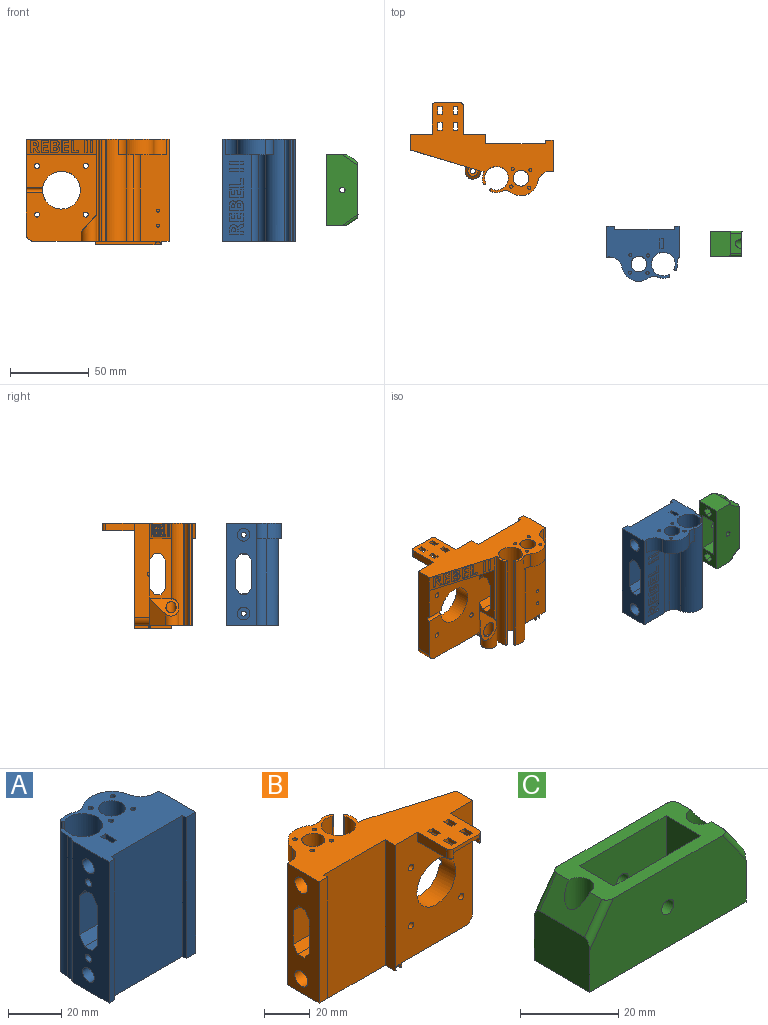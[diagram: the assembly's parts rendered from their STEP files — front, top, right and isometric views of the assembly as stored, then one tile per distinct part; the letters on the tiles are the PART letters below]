
ASSEMBLY  parts=3 mates=2
PART A: 158 faces, bbox 46x35x65 mm
  f0: plane 65x18.32mm, normal (0,1,0), area 818mm2, adj f6,f7,f8,f18,f19,f65,f66,f67
  f1: plane 65x19.5mm, normal (-1,0,0), area 955mm2, adj f8,f14,f18,f22,f39,f42,f53,f54
  f2: cylinder r=1.6mm len=3.2mm, axis (1,0,0), area 16.3mm2, adj f41,f44
  f3: cylinder r=1.6mm len=3.2mm, axis (1,0,0), area 16.3mm2, adj f40,f51
  f4: cylinder r=1.6mm len=8.88mm, axis (1,0,0), area 89.3mm2, adj f38,f43
  f5: cylinder r=1.6mm len=8.88mm, axis (1,0,0), area 89.3mm2, adj f36,f50
  f6: plane 65x19.5mm, normal (1,0,0), area 931mm2, adj f0,f8,f9,f18,f35,f37,f53,f54
  f7: cylinder r=5mm len=65mm, axis (0,0,-1), area 562.2mm2, adj f0,f8,f18,f19,f20
  f8: plane 46x33mm, normal (0,0,-1), area 837.7mm2, adj f0,f1,f6,f7,f9,f11,f12,f13
  f9: plane 65x5mm, normal (0,-1,0), area 325mm2, adj f6,f8,f17,f18
  f10: cylinder r=11mm len=17.47mm, axis (0,0,-1), area 223.9mm2, adj f18,f19,f21,f65
  f11: cylinder r=9mm len=65mm, axis (0,0,-1), area 971.4mm2, adj f8,f18,f19,f20,f21,f24
  f12: cylinder r=7.5mm len=65mm, axis (0,0,-1), area 2711.4mm2, adj f8,f18,f23,f26
  f13: cylinder r=9mm len=65mm, axis (0,0,-1), area 293.5mm2, adj f8,f18,f22,f25
  f14: plane 65x3mm, normal (0,-1,0), area 195mm2, adj f1,f8,f15,f18
  f15: plane 65x2mm, normal (1,0,0), area 130mm2, adj f8,f14,f16,f18
  f16: plane 65x38mm, normal (0,-1,0), area 2470mm2, adj f8,f15,f17,f18
  f17: plane 65x2mm, normal (-1,0,0), area 130mm2, adj f8,f9,f16,f18
  f18: plane 46x35mm, normal (0,0,1), area 1003.8mm2, adj f0,f1,f6,f7,f9,f10,f11,f12
  f19: plane 30.44x15.5mm, normal (0,0,-1), area 178.7mm2, adj f0,f7,f10,f11,f20,f21,f65
  f20: cylinder r=8mm len=55mm, axis (0,0,1), area 423.8mm2, adj f7,f8,f11,f19
  f21: cylinder r=5mm len=10mm, axis (0,0,1), area 53.9mm2, adj f10,f11,f18,f19
  f22: cylinder r=5mm len=65mm, axis (0,0,1), area 249.4mm2, adj f1,f8,f13,f18
  f23: cylinder r=1mm len=65mm, axis (0,0,-1), area 61mm2, adj f8,f12,f18,f24
  f24: cylinder r=1mm len=65mm, axis (0,0,-1), area 109.4mm2, adj f8,f11,f18,f23
  f25: cylinder r=1mm len=65mm, axis (0,0,-1), area 109.4mm2, adj f8,f13,f18,f26
  f26: cylinder r=1mm len=65mm, axis (0,0,-1), area 61mm2, adj f8,f12,f18,f25
  f27: cylinder r=1mm len=8mm, axis (0,0,1), area 50.3mm2, adj f18,f28
  f28: plane 2x2mm, normal (0,0,1), area 3.1mm2, adj f27
  f29: cylinder r=1mm len=8mm, axis (0,0,1), area 50.3mm2, adj f18,f30
  f30: plane 2x2mm, normal (0,0,1), area 3.1mm2, adj f29
  f31: cylinder r=1mm len=8mm, axis (0,0,1), area 50.3mm2, adj f18,f32
  f32: plane 2x2mm, normal (0,0,1), area 3.1mm2, adj f31
  f33: cylinder r=1mm len=8mm, axis (0,0,1), area 50.3mm2, adj f18,f34
  f34: plane 2x2mm, normal (0,0,1), area 3.1mm2, adj f33
  f35: cylinder r=4mm len=25mm, axis (1,0,0), area 628.3mm2, adj f6,f36
  f36: plane 8x8mm, normal (1,0,0), area 42.2mm2, adj f5,f35
  f37: cylinder r=4mm len=25mm, axis (1,0,0), area 628.3mm2, adj f6,f38
  f38: plane 8x8mm, normal (1,0,0), area 42.2mm2, adj f4,f37
  f39: cylinder r=3.1mm len=8mm, axis (-1,0,0), area 155.8mm2, adj f1,f40
  f40: plane 6.2x6.2mm, normal (-1,0,0), area 22.1mm2, adj f3,f39
  f41: plane 6.2x6.2mm, normal (-1,0,0), area 22.1mm2, adj f2,f42
  f42: cylinder r=3.1mm len=8mm, axis (-1,0,0), area 155.8mm2, adj f1,f41
  f43: plane 10.5x6mm, normal (-1,0,0), area 55mm2, adj f4,f18,f45,f46,f47
  f44: plane 10.5x6mm, normal (1,0,0), area 55mm2, adj f2,f18,f45,f46,f47
  f45: plane 10.5x2.5mm, normal (0,-1,0), area 26.3mm2, adj f18,f43,f44,f47
  f46: plane 10.5x2.5mm, normal (0,1,0), area 26.3mm2, adj f18,f43,f44,f47
  f47: plane 6x2.5mm, normal (0,0,1), area 15mm2, adj f43,f44,f45,f46
  f48: plane 10.5x2.5mm, normal (0,-1,0), area 26.3mm2, adj f8,f50,f51,f52
  f49: plane 10.5x2.5mm, normal (0,1,0), area 26.3mm2, adj f8,f50,f51,f52
  f50: plane 10.5x6mm, normal (-1,0,0), area 55mm2, adj f5,f8,f48,f49,f52
  f51: plane 10.5x6mm, normal (1,0,0), area 55mm2, adj f3,f8,f48,f49,f52
  f52: plane 6x2.5mm, normal (0,0,-1), area 15mm2, adj f48,f49,f50,f51
  f53: plane 46x17.98mm, normal (0,1,0), area 827.1mm2, adj f1,f6,f54,f58
  f54: plane 46x4.01mm, normal (0,0.8,0.6), area 230.4mm2, adj f1,f6,f53,f55
  f55: plane 46x4mm, normal (0,0,1), area 184mm2, adj f1,f6,f54,f56
  f56: plane 46x3.99mm, normal (0,-0.8,0.6), area 229.5mm2, adj f1,f6,f55,f57
  f57: plane 46x18.03mm, normal (0,-1,0), area 829.3mm2, adj f1,f6,f56,f59
  f58: plane 46x4.01mm, normal (0,0.8,-0.6), area 230.4mm2, adj f1,f6,f53,f60
  f59: plane 46x3.99mm, normal (0,-0.8,-0.6), area 229.5mm2, adj f1,f6,f57,f60
  f60: plane 46x4mm, normal (0,0,-1), area 184mm2, adj f1,f6,f58,f59
  f61: cylinder r=1.6mm len=10mm, axis (-1,0,0), area 100.5mm2, adj f1,f62
  f62: plane 3.2x3.2mm, normal (-1,0,0), area 8mm2, adj f61
  f63: cylinder r=1.6mm len=10mm, axis (-1,0,0), area 100.5mm2, adj f1,f64
  f64: plane 3.2x3.2mm, normal (-1,0,0), area 8mm2, adj f63
  f65: cylinder r=8mm len=10mm, axis (0,0,-1), area 110.8mm2, adj f0,f10,f18,f19
  f66: plane 5.02x0.5mm, normal (1,0,0), area 2.5mm2, adj f0,f67,f77,f78
  f67: plane 1.53x0.5mm, normal (0,0,-1), area 0.8mm2, adj f0,f66,f68,f78
  f68: plane 3.17x0.5mm, normal (-1,0,0), area 1.6mm2, adj f0,f67,f69,f78
  f69: plane 2.25x0.5mm, normal (0,0,-1), area 1.1mm2, adj f0,f68,f70,f78
  f70: plane 2.95x0.5mm, normal (1,0,0), area 1.5mm2, adj f0,f69,f71,f78
  f71: plane 1.52x0.5mm, normal (0,0,-1), area 0.8mm2, adj f0,f70,f72,f78
  f72: plane 2.95x0.5mm, normal (-1,0,0), area 1.5mm2, adj f0,f71,f73,f78
  f73: plane 1.92x0.5mm, normal (0,0,-1), area 1mm2, adj f0,f72,f74,f78
  f74: plane 3.17x0.5mm, normal (1,0,0), area 1.6mm2, adj f0,f73,f75,f78
  f75: plane 1.52x0.5mm, normal (0,0,-1), area 0.8mm2, adj f0,f74,f76,f78
  f76: plane 5.02x0.5mm, normal (-1,0,0), area 2.5mm2, adj f0,f75,f77,f78
  f77: plane 8.73x0.5mm, normal (0,0,1), area 4.4mm2, adj f0,f66,f76,f78
  f78: plane 8.73x5.02mm, normal (0,1,0), area 30.3mm2, adj f66,f67,f68,f69,f70,f71,f72,f73
  f79: plane 5.02x0.5mm, normal (1,0,0), area 2.5mm2, adj f0,f80,f90,f91
  f80: plane 1.53x0.5mm, normal (0,0,-1), area 0.8mm2, adj f0,f79,f81,f91
  f81: plane 3.17x0.5mm, normal (-1,0,0), area 1.6mm2, adj f0,f80,f82,f91
  f82: plane 2.25x0.5mm, normal (0,0,-1), area 1.1mm2, adj f0,f81,f83,f91
  f83: plane 2.95x0.5mm, normal (1,0,0), area 1.5mm2, adj f0,f82,f84,f91
  f84: plane 1.52x0.5mm, normal (0,0,-1), area 0.8mm2, adj f0,f83,f85,f91
  f85: plane 2.95x0.5mm, normal (-1,0,0), area 1.5mm2, adj f0,f84,f86,f91
  f86: plane 1.92x0.5mm, normal (0,0,-1), area 1mm2, adj f0,f85,f87,f91
  f87: plane 3.17x0.5mm, normal (1,0,0), area 1.6mm2, adj f0,f86,f88,f91
  f88: plane 1.52x0.5mm, normal (0,0,-1), area 0.8mm2, adj f0,f87,f89,f91
  f89: plane 5.02x0.5mm, normal (-1,0,0), area 2.5mm2, adj f0,f88,f90,f91
  f90: plane 8.73x0.5mm, normal (0,0,1), area 4.4mm2, adj f0,f79,f89,f91
  f91: plane 8.73x5.02mm, normal (0,1,0), area 30.3mm2, adj f79,f80,f81,f82,f83,f84,f85,f86
  f92: plane 8.73x0.5mm, normal (0,0,1), area 4.4mm2, adj f0,f93,f97,f98
  f93: plane 5.39x0.5mm, normal (1,0,0), area 2.7mm2, adj f0,f92,f94,f98
  f94: plane 1.53x0.5mm, normal (0,0,-1), area 0.8mm2, adj f0,f93,f95,f98
  f95: plane 3.54x0.5mm, normal (-1,0,0), area 1.8mm2, adj f0,f94,f96,f98
  f96: plane 7.2x0.5mm, normal (0,0,-1), area 3.6mm2, adj f0,f95,f97,f98
  f97: plane 1.85x0.5mm, normal (-1,0,0), area 0.9mm2, adj f0,f92,f96,f98
  f98: plane 8.73x5.39mm, normal (0,1,0), area 21.6mm2, adj f92,f93,f94,f95,f96,f97
  f99: plane 8.73x0.5mm, normal (0,0,1), area 4.4mm2, adj f0,f100,f102,f103
  f100: plane 1.85x0.5mm, normal (1,0,0), area 0.9mm2, adj f0,f99,f101,f103
  f101: plane 8.73x0.5mm, normal (0,0,-1), area 4.4mm2, adj f0,f100,f102,f103
  f102: plane 1.85x0.5mm, normal (-1,0,0), area 0.9mm2, adj f0,f99,f101,f103
  f103: plane 8.73x1.85mm, normal (0,1,0), area 16.1mm2, adj f99,f100,f101,f102
  f104: plane 8.73x0.5mm, normal (0,0,1), area 4.4mm2, adj f0,f105,f107,f108
  f105: plane 1.85x0.5mm, normal (1,0,0), area 0.9mm2, adj f0,f104,f106,f108
  f106: plane 8.73x0.5mm, normal (0,0,-1), area 4.4mm2, adj f0,f105,f107,f108
  f107: plane 1.85x0.5mm, normal (-1,0,0), area 0.9mm2, adj f0,f104,f106,f108
  f108: plane 8.73x1.85mm, normal (0,1,0), area 16.1mm2, adj f104,f105,f106,f107
  f109: plane 3.35x0.5mm, normal (0,0,-1), area 1.7mm2, adj f0,f110,f127,f128
  f110: plane 0.98x0.5mm, normal (1,0,0), area 0.5mm2, adj f0,f109,f111,f128
  f111: plane 3.35x2.08mm, normal (0.53,0,0.85), area 2mm2, adj f0,f110,f112,f128
  f112: plane 2.05x0.5mm, normal (1,0,0), area 1mm2, adj f0,f111,f113,f128
  f113: extruded ~3.8x2.57mm, area 2.3mm2, adj f0,f112,f114,f128
  f114: extruded ~1.2x0.94mm, area 0.8mm2, adj f0,f113,f115,f128
  f115: extruded ~1.37x0.5mm, area 0.7mm2, adj f0,f114,f116,f128
  f116: extruded ~1.97x0.85mm, area 1.1mm2, adj f0,f115,f117,f128
  f117: extruded ~2.63x0.65mm, area 1.4mm2, adj f0,f116,f118,f128
  f118: plane 2.54x0.5mm, normal (-1,0,0), area 1.3mm2, adj f0,f117,f119,f128
  f119: plane 8.73x0.5mm, normal (0,0,1), area 4.4mm2, adj f0,f118,f127,f128
  f120: plane 0.6x0.5mm, normal (-1,0,0), area 0.3mm2, adj f121,f126,f128,f129
  f121: plane 2.36x0.5mm, normal (0,0,-1), area 1.2mm2, adj f120,f122,f128,f129
  f122: plane 0.56x0.5mm, normal (1,0,0), area 0.3mm2, adj f121,f123,f128,f129
  f123: extruded ~1.32x0.5mm, area 0.7mm2, adj f122,f124,f128,f129
  f124: extruded ~0.88x0.5mm, area 0.5mm2, adj f123,f125,f128,f129
  f125: extruded ~0.92x0.5mm, area 0.5mm2, adj f124,f126,f128,f129
  f126: extruded ~1.3x0.5mm, area 0.7mm2, adj f120,f125,f128,f129
  f127: plane 1.85x0.5mm, normal (1,0,0), area 0.9mm2, adj f0,f109,f119,f128
  f128: plane 8.73x6.97mm, normal (0,1,0), area 37.2mm2, adj f109,f110,f111,f112,f113,f114,f115,f116
  f129: plane 2.36x2.31mm, normal (0,1,0), area 4.8mm2, adj f120,f121,f122,f123,f124,f125,f126
  f130: plane 2.27x0.5mm, normal (0,0,-1), area 1.1mm2, adj f131,f154,f155,f157
  f131: plane 1.15x0.5mm, normal (1,0,0), area 0.6mm2, adj f130,f132,f155,f157
  f132: extruded ~1.55x1.09mm, area 1.1mm2, adj f131,f133,f155,f157
  f133: extruded ~0.9x0.5mm, area 0.5mm2, adj f132,f134,f155,f157
  f134: extruded ~1.13x0.5mm, area 0.6mm2, adj f133,f154,f155,f157
  f135: plane 1.07x0.5mm, normal (-1,0,0), area 0.5mm2, adj f136,f152,f155,f156
  f136: plane 1.94x0.5mm, normal (0,0,-1), area 1mm2, adj f135,f137,f155,f156
  f137: plane 0.97x0.5mm, normal (1,0,0), area 0.5mm2, adj f136,f138,f155,f156
  f138: extruded ~1.16x0.5mm, area 0.6mm2, adj f137,f139,f155,f156
  f139: extruded ~0.72x0.5mm, area 0.4mm2, adj f138,f140,f155,f156
  f140: extruded ~0.77x0.5mm, area 0.4mm2, adj f139,f152,f155,f156
  f141: plane 2.72x0.5mm, normal (-1,0,0), area 1.4mm2, adj f0,f142,f153,f155
  f142: plane 8.73x0.5mm, normal (0,0,1), area 4.4mm2, adj f0,f141,f143,f155
  f143: plane 3.26x0.5mm, normal (1,0,0), area 1.6mm2, adj f0,f142,f144,f155
  f144: extruded ~2.34x0.67mm, area 1.2mm2, adj f0,f143,f145,f155
  f145: extruded ~1.86x0.86mm, area 1.1mm2, adj f0,f144,f146,f155
  f146: extruded ~1.35x0.5mm, area 0.7mm2, adj f0,f145,f147,f155
  f147: extruded ~1.2x0.69mm, area 0.7mm2, adj f0,f146,f148,f155
  f148: plane 0.5x0.06mm, normal (0,0,-1), area 0mm2, adj f0,f147,f149,f155
  f149: extruded ~0.98x0.6mm, area 0.6mm2, adj f0,f148,f150,f155
  f150: extruded ~1.28x0.5mm, area 0.7mm2, adj f0,f149,f151,f155
  f151: extruded ~1.68x0.84mm, area 1mm2, adj f0,f150,f153,f155
  f152: extruded ~1.09x0.5mm, area 0.6mm2, adj f135,f140,f155,f156
  f153: extruded ~2.69x0.53mm, area 1.4mm2, adj f0,f141,f151,f155
  f154: plane 1.21x0.5mm, normal (-1,0,0), area 0.6mm2, adj f130,f134,f155,f157
  f155: plane 8.73x6.47mm, normal (0,1,0), area 41.5mm2, adj f130,f131,f132,f133,f134,f135,f136,f137
  f156: plane 2.5x1.94mm, normal (0,1,0), area 4.4mm2, adj f135,f136,f137,f138,f139,f140,f152
  f157: plane 2.7x2.27mm, normal (0,1,0), area 5.6mm2, adj f130,f131,f132,f133,f134,f154
PART B: 213 faces, bbox 92.5x60.6x69.2 mm
  f0: plane 39x23.85mm, normal (0,0,-1), area 44.3mm2, adj f1,f20,f23,f24,f194,f197,f198,f202
  f1: plane 67.3x48mm, normal (0,-1,0), area 2581.9mm2, adj f0,f3,f4,f7,f8,f15,f24,f25
  f2: plane 1.73x0.24mm, normal (-1,0,0), area 0.3mm2, adj f3,f197,f203,f204,f205
  f3: plane 39.1x23.87mm, normal (0,0,-1), area 44.1mm2, adj f1,f2,f20,f195,f196,f197,f199,f202
  f4: plane 39x10mm, normal (0,0,-1), area 390mm2, adj f1,f17,f76,f199
  f5: plane 47x27mm, normal (0,0,-1), area 619.3mm2, adj f10,f11,f19,f20,f26,f27,f28,f29
  f6: plane 19.5x5mm, normal (0,0,-1), area 97.5mm2, adj f18,f20,f21,f22,f194
  f7: plane 91x59.06mm, normal (0,0,1), area 2120.1mm2, adj f1,f9,f14,f18,f19,f20,f21,f22
  f8: plane 20x16mm, normal (0,0,-1), area 260mm2, adj f1,f14,f69,f70,f178,f179,f180,f181
  f9: plane 45x13.5mm, normal (0.29,0.96,0), area 301.8mm2, adj f7,f25,f26,f63,f86,f87,f88,f89
  f10: plane 17x10.24mm, normal (0.76,-0.65,0), area 163.6mm2, adj f5,f11,f17,f85,f200
  f11: cylinder r=5mm len=17mm, axis (0,0,-1), area 202.3mm2, adj f5,f10,f26,f85
  f12: cylinder r=3.25mm len=10.06mm, axis (0,0,1), area 131.6mm2, adj f84,f85
  f13: cylinder r=1.6mm len=3.2mm, axis (0,0,-1), area 20.1mm2, adj f77,f84
  f14: plane 16x2mm, normal (0,-1,0), area 32mm2, adj f7,f8,f67,f68
  f15: plane 20x2mm, normal (0,0,-1), area 39.1mm2, adj f1,f65,f68,f70
  f16: plane 38x13.5mm, normal (1,0,0), area 277mm2, adj f17,f26,f51,f52,f53,f54,f55,f56
  f17: plane 91x55mm, normal (0,1,0), area 2781.5mm2, adj f4,f10,f16,f18,f25,f51,f57,f58
  f18: plane 65x19.5mm, normal (-1,0,0), area 931mm2, adj f6,f7,f17,f20,f21,f47,f49,f51
  f19: cylinder r=5mm len=65mm, axis (0,0,-1), area 548mm2, adj f5,f7,f20,f31,f32
  f20: plane 67.3x18.44mm, normal (0,1,0), area 1029.3mm2, adj f0,f3,f5,f6,f7,f18,f19,f31
  f21: plane 65x5mm, normal (0,-1,0), area 325mm2, adj f6,f7,f18,f22
  f22: plane 65x2.06mm, normal (1,0,0), area 133.6mm2, adj f6,f7,f21,f23
  f23: plane 67.3x38mm, normal (0,-1,0), area 2557.4mm2, adj f0,f7,f22,f24,f194
  f24: plane 67.3x6.06mm, normal (-1,0,0), area 407.5mm2, adj f0,f1,f7,f23
  f25: plane 60x10mm, normal (1,0,0), area 596.5mm2, adj f1,f7,f9,f17,f75,f76
  f26: plane 65x2.24mm, normal (0,1,0), area 145.5mm2, adj f5,f7,f9,f11,f16,f27
  f27: cylinder r=9mm len=65mm, axis (0,0,-1), area 538.6mm2, adj f5,f7,f26,f44
  f28: cylinder r=7.5mm len=65mm, axis (0,0,-1), area 2711.3mm2, adj f5,f7,f43,f46
  f29: cylinder r=9mm len=65mm, axis (0,0,-1), area 977.8mm2, adj f5,f7,f31,f32,f33,f45
  f30: cylinder r=11mm len=17.48mm, axis (0,0,-1), area 224.3mm2, adj f7,f31,f33,f34
  f31: plane 30.45x15.56mm, normal (0,0,-1), area 179.2mm2, adj f19,f20,f29,f30,f32,f33,f34
  f32: cylinder r=8mm len=55mm, axis (0,0,1), area 430.9mm2, adj f5,f19,f29,f31
  f33: cylinder r=5mm len=10mm, axis (0,0,1), area 53.9mm2, adj f7,f29,f30,f31
  f34: cylinder r=8mm len=10mm, axis (0,0,-1), area 111.1mm2, adj f7,f20,f30,f31
  f35: cylinder r=1mm len=8mm, axis (0,0,1), area 50.3mm2, adj f7,f36
  f36: plane 2x2mm, normal (0,0,1), area 3.1mm2, adj f35
  f37: cylinder r=1mm len=8mm, axis (0,0,1), area 50.3mm2, adj f7,f38
  f38: plane 2x2mm, normal (0,0,1), area 3.1mm2, adj f37
  f39: cylinder r=1mm len=8mm, axis (0,0,1), area 50.3mm2, adj f7,f40
  f40: plane 2x2mm, normal (0,0,1), area 3.1mm2, adj f39
  f41: cylinder r=1mm len=8mm, axis (0,0,1), area 50.3mm2, adj f7,f42
  f42: plane 2x2mm, normal (0,0,1), area 3.1mm2, adj f41
  f43: cylinder r=1mm len=65mm, axis (0,0,-1), area 60.2mm2, adj f5,f7,f28,f44
  f44: cylinder r=1mm len=65mm, axis (0,0,-1), area 110.1mm2, adj f5,f7,f27,f43
  f45: cylinder r=1mm len=65mm, axis (0,0,-1), area 108.8mm2, adj f5,f7,f29,f46
  f46: cylinder r=1mm len=65mm, axis (0,0,-1), area 61.7mm2, adj f5,f7,f28,f45
  f47: cylinder r=4mm len=25mm, axis (-1,0,0), area 628.3mm2, adj f18,f48
  f48: plane 8x8mm, normal (-1,0,0), area 50.3mm2, adj f47
  f49: cylinder r=4mm len=25mm, axis (-1,0,0), area 628.3mm2, adj f18,f50
  f50: plane 8x8mm, normal (-1,0,0), area 50.3mm2, adj f49
  f51: plane 46x4mm, normal (0,0.81,-0.59), area 227.8mm2, adj f16,f17,f18,f52
  f52: plane 46x4mm, normal (0,0,-1), area 184mm2, adj f16,f18,f51,f53
  f53: plane 46x4mm, normal (0,-0.79,-0.61), area 232.2mm2, adj f16,f18,f52,f54
  f54: plane 46x18mm, normal (0,-1,0), area 828mm2, adj f16,f18,f53,f55
  f55: plane 46x4mm, normal (0,-0.81,0.59), area 227.8mm2, adj f16,f18,f54,f56
  f56: plane 46x4mm, normal (0,0,1), area 184mm2, adj f16,f18,f55,f57
  f57: plane 46x4mm, normal (0,0.79,0.61), area 232.2mm2, adj f16,f17,f18,f56
  f58: cylinder r=1.6mm len=10mm, axis (0,-1,0), area 100.5mm2, adj f1,f17
  f59: cylinder r=1.6mm len=10mm, axis (0,-1,0), area 100.5mm2, adj f1,f17
  f60: cylinder r=12mm len=24mm, axis (0,-1,0), area 754mm2, adj f1,f17,f75
  f61: cylinder r=1.6mm len=10mm, axis (0,-1,0), area 100.5mm2, adj f1,f17
  f62: cylinder r=1.6mm len=10mm, axis (0,-1,0), area 100.5mm2, adj f1,f17
  f63: plane 45x13.5mm, normal (0,0,-1), area 303.8mm2, adj f9,f16,f17
  f64: plane 18x5mm, normal (-1,0,0), area 90mm2, adj f1,f7,f66,f67
  f65: plane 18x5mm, normal (1,0,0), area 90mm2, adj f1,f7,f15,f68
  f66: plane 20x2mm, normal (0,0,-1), area 39.1mm2, adj f1,f64,f67,f69
  f67: cylinder r=2mm len=5mm, axis (0,0,1), area 15.7mm2, adj f7,f14,f64,f66,f69
  f68: cylinder r=2mm len=5mm, axis (0,0,1), area 15.7mm2, adj f7,f14,f15,f65,f70
  f69: plane 20x3mm, normal (1,0,0), area 60mm2, adj f1,f8,f66,f67
  f70: plane 20x3mm, normal (-1,0,0), area 60mm2, adj f1,f8,f15,f68
  f71: cylinder r=1mm len=4mm, axis (0,1,0), area 25.1mm2, adj f20,f72
  f72: plane 2x2mm, normal (0,1,0), area 3.1mm2, adj f71
  f73: cylinder r=1mm len=4mm, axis (0,1,0), area 25.1mm2, adj f20,f74
  f74: plane 2x2mm, normal (0,1,0), area 3.1mm2, adj f73
  f75: cylinder r=1.5mm len=10.59mm, axis (1,0,0), area 49.9mm2, adj f17,f25,f60
  f76: cylinder r=5mm len=10mm, axis (0,1,0), area 78.5mm2, adj f1,f4,f17,f25
  f77: plane 5.98x5.83mm, normal (0,0,-1), area 16.3mm2, adj f13,f78,f79,f80,f81,f82,f83
  f78: plane 3x2.99mm, normal (-0.21,-0.98,0), area 9.2mm2, adj f5,f77,f79,f83
  f79: plane 3x2.92mm, normal (-0.95,-0.3,0), area 9.2mm2, adj f5,f77,f78,f80
  f80: plane 3x2.26mm, normal (-0.74,0.67,0), area 9.2mm2, adj f5,f77,f79,f81
  f81: plane 3x2.99mm, normal (0.21,0.98,0), area 9.2mm2, adj f5,f77,f80,f82
  f82: plane 3x2.92mm, normal (0.95,0.3,0), area 9.2mm2, adj f5,f77,f81,f83
  f83: plane 3x2.26mm, normal (0.74,-0.67,0), area 9.2mm2, adj f5,f77,f78,f82
  f84: plane 6.5x6.5mm, normal (0,0,1), area 25.1mm2, adj f12,f13
  f85: plane 20.02x12.62mm, normal (0.74,0,0.67), area 123.2mm2, adj f10,f11,f12,f16
  f86: plane 4.47x1.78mm, normal (0,0,1), area 2.3mm2, adj f9,f87,f97,f98
  f87: plane 1.37x0.48mm, normal (0.96,-0.29,0), area 0.7mm2, adj f9,f86,f88,f98
  f88: plane 2.88x1.3mm, normal (0,0,-1), area 1.4mm2, adj f9,f87,f89,f98
  f89: plane 2.02x0.48mm, normal (0.96,-0.29,0), area 1mm2, adj f9,f88,f90,f98
  f90: plane 2.69x1.24mm, normal (0,0,1), area 1.3mm2, adj f9,f89,f91,f98
  f91: plane 1.36x0.48mm, normal (0.96,-0.29,0), area 0.7mm2, adj f9,f90,f92,f98
  f92: plane 2.69x1.24mm, normal (0,0,-1), area 1.3mm2, adj f9,f91,f93,f98
  f93: plane 1.72x0.48mm, normal (0.96,-0.29,0), area 0.9mm2, adj f9,f92,f94,f98
  f94: plane 2.88x1.3mm, normal (0,0,1), area 1.4mm2, adj f9,f93,f95,f98
  f95: plane 1.36x0.48mm, normal (0.96,-0.29,0), area 0.7mm2, adj f9,f94,f96,f98
  f96: plane 4.47x1.78mm, normal (0,0,-1), area 2.3mm2, adj f9,f95,f97,f98
  f97: plane 7.84x0.48mm, normal (-0.96,0.29,0), area 3.9mm2, adj f9,f86,f96,f98
  f98: plane 7.84x4.33mm, normal (0.29,0.96,0), area 24.5mm2, adj f86,f87,f88,f89,f90,f91,f92,f93
  f99: plane 4.47x1.78mm, normal (0,0,1), area 2.3mm2, adj f9,f100,f110,f111
  f100: plane 1.37x0.48mm, normal (0.96,-0.29,0), area 0.7mm2, adj f9,f99,f101,f111
  f101: plane 2.88x1.3mm, normal (0,0,-1), area 1.4mm2, adj f9,f100,f102,f111
  f102: plane 2.02x0.48mm, normal (0.96,-0.29,0), area 1mm2, adj f9,f101,f103,f111
  f103: plane 2.69x1.24mm, normal (0,0,1), area 1.3mm2, adj f9,f102,f104,f111
  f104: plane 1.36x0.48mm, normal (0.96,-0.29,0), area 0.7mm2, adj f9,f103,f105,f111
  f105: plane 2.69x1.24mm, normal (0,0,-1), area 1.3mm2, adj f9,f104,f106,f111
  f106: plane 1.72x0.48mm, normal (0.96,-0.29,0), area 0.9mm2, adj f9,f105,f107,f111
  f107: plane 2.88x1.3mm, normal (0,0,1), area 1.4mm2, adj f9,f106,f108,f111
  f108: plane 1.36x0.48mm, normal (0.96,-0.29,0), area 0.7mm2, adj f9,f107,f109,f111
  f109: plane 4.47x1.78mm, normal (0,0,-1), area 2.3mm2, adj f9,f108,f110,f111
  f110: plane 7.84x0.48mm, normal (-0.96,0.29,0), area 3.9mm2, adj f9,f99,f109,f111
  f111: plane 7.84x4.33mm, normal (0.29,0.96,0), area 24.5mm2, adj f99,f100,f101,f102,f103,f104,f105,f106
  f112: plane 7.84x0.48mm, normal (-0.96,0.29,0), area 3.9mm2, adj f9,f113,f117,f118
  f113: plane 4.78x1.87mm, normal (0,0,1), area 2.4mm2, adj f9,f112,f114,f118
  f114: plane 1.37x0.48mm, normal (0.96,-0.29,0), area 0.7mm2, adj f9,f113,f115,f118
  f115: plane 3.19x1.39mm, normal (0,0,-1), area 1.6mm2, adj f9,f114,f116,f118
  f116: plane 6.47x0.48mm, normal (0.96,-0.29,0), area 3.2mm2, adj f9,f115,f117,f118
  f117: plane 1.74x0.96mm, normal (0,0,-1), area 0.8mm2, adj f9,f112,f116,f118
  f118: plane 7.84x4.64mm, normal (0.29,0.96,0), area 17.4mm2, adj f112,f113,f114,f115,f116,f117
  f119: plane 7.84x0.48mm, normal (-0.96,0.29,0), area 3.9mm2, adj f9,f120,f122,f123
  f120: plane 1.74x0.96mm, normal (0,0,1), area 0.8mm2, adj f9,f119,f121,f123
  f121: plane 7.84x0.48mm, normal (0.96,-0.29,0), area 3.9mm2, adj f9,f120,f122,f123
  f122: plane 1.74x0.96mm, normal (0,0,-1), area 0.8mm2, adj f9,f119,f121,f123
  f123: plane 7.84x1.59mm, normal (0.29,0.96,0), area 13mm2, adj f119,f120,f121,f122
  f124: plane 7.84x0.48mm, normal (-0.96,0.29,0), area 3.9mm2, adj f9,f125,f127,f128
  f125: plane 1.74x0.96mm, normal (0,0,1), area 0.8mm2, adj f9,f124,f126,f128
  f126: plane 7.84x0.48mm, normal (0.96,-0.29,0), area 3.9mm2, adj f9,f125,f127,f128
  f127: plane 1.74x0.96mm, normal (0,0,-1), area 0.8mm2, adj f9,f124,f126,f128
  f128: plane 7.84x1.59mm, normal (0.29,0.96,0), area 13mm2, adj f124,f125,f126,f127
  f129: plane 3.01x0.48mm, normal (0.96,-0.29,0), area 1.5mm2, adj f9,f130,f147,f148
  f130: plane 0.99x0.73mm, normal (0,0,1), area 0.4mm2, adj f9,f129,f131,f148
  f131: plane 3.01x1.94mm, normal (-0.81,0.24,0.53), area 1.8mm2, adj f9,f130,f132,f148
  f132: plane 1.91x1.01mm, normal (0,0,1), area 0.9mm2, adj f9,f131,f133,f148
  f133: extruded ~3.42x2.35mm, area 2.1mm2, adj f9,f132,f134,f148
  f134: extruded ~1.18x0.84mm, area 0.7mm2, adj f9,f133,f135,f148
  f135: extruded ~1.23x0.59mm, area 0.7mm2, adj f9,f134,f136,f148
  f136: extruded ~1.77x0.88mm, area 1mm2, adj f9,f135,f137,f148
  f137: extruded ~2.41x1.16mm, area 1.2mm2, adj f9,f136,f138,f148
  f138: plane 2.33x1.14mm, normal (0,0,-1), area 1.1mm2, adj f9,f137,f139,f148
  f139: plane 7.84x0.48mm, normal (-0.96,0.29,0), area 3.9mm2, adj f9,f138,f147,f148
  f140: plane 0.66x0.63mm, normal (0,0,-1), area 0.3mm2, adj f141,f146,f148,f149
  f141: plane 2.12x0.48mm, normal (0.96,-0.29,0), area 1.1mm2, adj f140,f142,f148,f149
  f142: plane 0.63x0.62mm, normal (0,0,1), area 0.3mm2, adj f141,f143,f148,f149
  f143: extruded ~1.28x0.82mm, area 0.6mm2, adj f142,f144,f148,f149
  f144: extruded ~0.79x0.59mm, area 0.5mm2, adj f143,f145,f148,f149
  f145: extruded ~0.83x0.59mm, area 0.5mm2, adj f144,f146,f148,f149
  f146: extruded ~1.26x0.81mm, area 0.6mm2, adj f140,f145,f148,f149
  f147: plane 1.74x0.96mm, normal (0,0,1), area 0.8mm2, adj f9,f129,f139,f148
  f148: plane 7.84x6mm, normal (0.29,0.96,0), area 30mm2, adj f129,f130,f131,f132,f133,f134,f135,f136
  f149: plane 2.12x1.99mm, normal (0.29,0.96,0), area 3.9mm2, adj f140,f141,f142,f143,f144,f145,f146
  f150: plane 2.04x0.48mm, normal (0.96,-0.29,0), area 1mm2, adj f151,f174,f175,f177
  f151: plane 1.13x0.78mm, normal (0,0,1), area 0.5mm2, adj f150,f152,f175,f177
  f152: extruded ~1.48x0.98mm, area 1mm2, adj f151,f153,f175,f177
  f153: extruded ~0.81x0.57mm, area 0.5mm2, adj f152,f154,f175,f177
  f154: extruded ~1.11x0.77mm, area 0.5mm2, adj f153,f174,f175,f177
  f155: plane 1.07x0.76mm, normal (0,0,-1), area 0.5mm2, adj f156,f172,f175,f176
  f156: plane 1.74x0.48mm, normal (0.96,-0.29,0), area 0.9mm2, adj f155,f157,f175,f176
  f157: plane 0.98x0.73mm, normal (0,0,1), area 0.4mm2, adj f156,f158,f175,f176
  f158: extruded ~1.14x0.78mm, area 0.5mm2, adj f157,f159,f175,f176
  f159: extruded ~0.65x0.57mm, area 0.4mm2, adj f158,f160,f175,f176
  f160: extruded ~0.69x0.57mm, area 0.4mm2, adj f159,f172,f175,f176
  f161: plane 2.48x1.18mm, normal (0,0,-1), area 1.2mm2, adj f9,f162,f173,f175
  f162: plane 7.84x0.48mm, normal (-0.96,0.29,0), area 3.9mm2, adj f9,f161,f163,f175
  f163: plane 2.95x1.32mm, normal (0,0,1), area 1.5mm2, adj f9,f162,f164,f175
  f164: extruded ~2.16x1.08mm, area 1.1mm2, adj f9,f163,f165,f175
  f165: extruded ~1.67x0.89mm, area 1mm2, adj f9,f164,f166,f175
  f166: extruded ~1.21x0.57mm, area 0.6mm2, adj f9,f165,f167,f175
  f167: extruded ~1.17x0.79mm, area 0.6mm2, adj f9,f166,f168,f175
  f168: plane 0.48x0.14mm, normal (0.96,-0.29,0), area 0mm2, adj f9,f167,f169,f175
  f169: extruded ~0.98x0.73mm, area 0.5mm2, adj f9,f168,f170,f175
  f170: extruded ~1.15x0.57mm, area 0.6mm2, adj f9,f169,f171,f175
  f171: extruded ~1.51x0.87mm, area 0.9mm2, adj f9,f170,f173,f175
  f172: extruded ~1.08x0.76mm, area 0.5mm2, adj f155,f160,f175,f176
  f173: extruded ~2.46x1.18mm, area 1.2mm2, adj f9,f161,f171,f175
  f174: plane 1.18x0.79mm, normal (0,0,-1), area 0.5mm2, adj f150,f154,f175,f177
  f175: plane 7.84x5.57mm, normal (0.29,0.96,0), area 33.5mm2, adj f150,f151,f152,f153,f154,f155,f156,f157
  f176: plane 2.15x1.74mm, normal (0.29,0.96,0), area 3.6mm2, adj f155,f156,f157,f158,f159,f160,f172
  f177: plane 2.32x2.04mm, normal (0.29,0.96,0), area 4.5mm2, adj f150,f151,f152,f153,f154,f174
  f178: plane 3x2mm, normal (0,1,0), area 6mm2, adj f7,f8,f179,f181
  f179: plane 5x2mm, normal (-1,0,0), area 10mm2, adj f7,f8,f178,f180
  f180: plane 3x2mm, normal (0,-1,0), area 6mm2, adj f7,f8,f179,f181
  f181: plane 5x2mm, normal (1,0,0), area 10mm2, adj f7,f8,f178,f180
  f182: plane 5x2mm, normal (1,0,0), area 10mm2, adj f7,f8,f183,f184
  f183: plane 3x2mm, normal (0,-1,0), area 6mm2, adj f7,f8,f182,f185
  f184: plane 3x2mm, normal (0,1,0), area 6mm2, adj f7,f8,f182,f185
  f185: plane 5x2mm, normal (-1,0,0), area 10mm2, adj f7,f8,f183,f184
  f186: plane 3x2mm, normal (0,-1,0), area 6mm2, adj f7,f8,f187,f189
  f187: plane 5x2mm, normal (1,0,0), area 10mm2, adj f7,f8,f186,f188
  f188: plane 3x2mm, normal (0,1,0), area 6mm2, adj f7,f8,f187,f189
  f189: plane 5x2mm, normal (-1,0,0), area 10mm2, adj f7,f8,f186,f188
  f190: plane 5x2mm, normal (-1,0,0), area 10mm2, adj f7,f8,f191,f193
  f191: plane 3x2mm, normal (0,-1,0), area 6mm2, adj f7,f8,f190,f192
  f192: plane 5x2mm, normal (1,0,0), area 10mm2, adj f7,f8,f191,f193
  f193: plane 3x2mm, normal (0,1,0), area 6mm2, adj f7,f8,f190,f192
  f194: plane 17.45x2.3mm, normal (-1,0,0), area 40.1mm2, adj f0,f6,f20,f23
  f195: plane 13.45x2.3mm, normal (1,0,0), area 30.9mm2, adj f3,f5,f20,f196
  f196: plane 38x2.3mm, normal (0,1,0), area 87.4mm2, adj f3,f5,f195,f199,f200
  f197: cylinder r=1.5mm len=39.27mm, axis (1,0,0), area 236mm2, adj f0,f2,f3,f198,f201,f205,f206,f207
  f198: plane 4.09x2.41mm, normal (1,0,0), area 6.8mm2, adj f0,f197,f209,f210,f211
  f199: plane 10.06x2.3mm, normal (1,0,0), area 23.1mm2, adj f1,f3,f4,f196,f200
  f200: plane 1x0.06mm, normal (0,0,1), area 0.1mm2, adj f10,f17,f196,f199
  f201: plane 0.79x0.05mm, normal (-1,0,0), area 0mm2, adj f197,f207
  f202: cylinder r=1.5mm len=8.82mm, axis (0,-1,0), area 46.3mm2, adj f0,f1,f3,f204,f206,f207
  f203: plane 1.65x1mm, normal (0,-1,0), area 1.4mm2, adj f2,f3,f204
  f204: torus R=1mm, axis (0,-1,0), area 2.5mm2, adj f2,f3,f202,f203,f205,f208
  f205: bspline ~1.15x0.83mm, area 0.6mm2, adj f2,f197,f204,f207,f208
  f206: bspline ~2.83x2.45mm, area 3.8mm2, adj f0,f197,f202,f207
  f207: cylinder r=0.1mm len=1.63mm, axis (0,-1,0), area 0.2mm2, adj f197,f201,f202,f205,f206,f208
  f208: bspline ~0.22x0.11mm, area 0mm2, adj f204,f205,f207
  f209: cylinder r=1.5mm len=15.45mm, axis (0,1,0), area 87.5mm2, adj f0,f3,f20,f198,f210,f211,f212
  f210: bspline ~1.97x1.97mm, area 0.6mm2, adj f197,f198,f209
  f211: bspline ~1.9x1.12mm, area 0.9mm2, adj f0,f198,f209
  f212: bspline ~2.5x2.5mm, area 3.9mm2, adj f3,f197,f209
PART C: 38 faces, bbox 47.4x16x20.9 mm
  f0: cylinder r=1.75mm len=4mm, axis (0,0,-1), area 44mm2, adj f27,f31
  f1: cylinder r=1.75mm len=4mm, axis (0,0,-1), area 44mm2, adj f14,f29
  f2: plane 35x16mm, normal (0,0,1), area 279.4mm2, adj f4,f6,f7,f8,f9,f10,f28,f30
  f3: plane 45x16mm, normal (0,0,-1), area 417.6mm2, adj f4,f5,f6,f7,f8,f9,f10,f11
  f4: plane 45x20mm, normal (0,1,0), area 824.8mm2, adj f2,f3,f5,f11,f13,f34,f35
  f5: plane 16x13mm, normal (-1,0,0), area 206.3mm2, adj f3,f4,f6,f32,f34,f36
  f6: plane 45x20mm, normal (0,-1,0), area 824.8mm2, adj f2,f3,f5,f11,f12,f36,f37
  f7: plane 20x10mm, normal (1,0,0), area 200mm2, adj f2,f3,f8,f10
  f8: plane 25x20mm, normal (0,-1,0), area 490.4mm2, adj f2,f3,f7,f9,f13
  f9: plane 20x10mm, normal (-1,0,0), area 200mm2, adj f2,f3,f8,f10
  f10: plane 25x20mm, normal (0,1,0), area 490.4mm2, adj f2,f3,f7,f9,f12
  f11: plane 16x13mm, normal (1,0,0), area 206.3mm2, adj f3,f4,f6,f33,f35,f37
  f12: cylinder r=1.75mm len=3.5mm, axis (0,-1,0), area 33mm2, adj f6,f10
  f13: cylinder r=1.75mm len=3.5mm, axis (0,-1,0), area 33mm2, adj f4,f8
  f14: plane 6.35x5.51mm, normal (0,0,-1), area 16.6mm2, adj f1,f15,f16,f17,f18,f19,f20
  f15: plane 5x3.18mm, normal (-1,0,0), area 15.9mm2, adj f3,f14,f16,f20
  f16: plane 5x2.76mm, normal (-0.5,0.87,0), area 15.9mm2, adj f3,f14,f15,f17
  f17: plane 5x2.74mm, normal (0.5,0.86,0), area 15.9mm2, adj f3,f14,f16,f18
  f18: plane 5x3.18mm, normal (1,0,0), area 15.9mm2, adj f3,f14,f17,f19
  f19: plane 5x2.76mm, normal (0.5,-0.87,0), area 15.9mm2, adj f3,f14,f18,f20
  f20: plane 5x2.74mm, normal (-0.5,-0.86,0), area 15.9mm2, adj f3,f14,f15,f19
  f21: plane 5x3.18mm, normal (1,0,0), area 15.9mm2, adj f3,f22,f26,f27
  f22: plane 5x2.74mm, normal (0.5,-0.86,0), area 15.9mm2, adj f3,f21,f23,f27
  f23: plane 5x2.76mm, normal (-0.5,-0.87,0), area 15.9mm2, adj f3,f22,f24,f27
  f24: plane 5x3.18mm, normal (-1,0,0), area 15.9mm2, adj f3,f23,f25,f27
  f25: plane 5x2.74mm, normal (-0.5,0.86,0), area 15.9mm2, adj f3,f24,f26,f27
  f26: plane 5x2.76mm, normal (0.5,0.87,0), area 15.9mm2, adj f3,f21,f25,f27
  f27: plane 6.35x5.51mm, normal (0,0,-1), area 16.6mm2, adj f0,f21,f22,f23,f24,f25,f26
  f28: cylinder r=3mm len=11mm, axis (0,0,1), area 182.1mm2, adj f2,f29,f32
  f29: plane 6x6mm, normal (0,0,1), area 18.7mm2, adj f1,f28
  f30: cylinder r=3mm len=11mm, axis (0,0,1), area 182.1mm2, adj f2,f31,f33
  f31: plane 6x6mm, normal (0,0,1), area 18.7mm2, adj f0,f30
  f32: plane 13x7mm, normal (-0.81,0,0.58), area 87.5mm2, adj f2,f5,f28,f34,f36
  f33: plane 13x7mm, normal (0.81,0,0.58), area 87.5mm2, adj f2,f11,f30,f35,f37
  f34: cylinder r=1.5mm len=10.45mm, axis (0.58,0,0.81), area 23mm2, adj f2,f4,f5,f32
  f35: cylinder r=1.5mm len=10.45mm, axis (-0.58,0,0.81), area 23mm2, adj f2,f4,f11,f33
  f36: cylinder r=1.5mm len=10.45mm, axis (0.58,0,0.81), area 23mm2, adj f2,f5,f6,f32
  f37: cylinder r=1.5mm len=10.45mm, axis (-0.58,0,0.81), area 23mm2, adj f2,f6,f11,f33
PLACE A rot(axis=(0,0,1),180deg) t=(-75.65,-116.83,49.49)mm
PLACE B rot(axis=(0,0,1),180deg) t=(-152.03,-57.34,49.49)mm
PLACE C rot(axis=(0,1,0),90deg) t=(-19.03,-113.17,49.59)mm
MATE pin_slot B.f49 <-> A.f2  axis (1,0,0) through (-129.03,-58.59,74.49)mm
MATE pin_slot A.f63 <-> C.f0  axis (1,0,0) through (-49.03,-113.17,32.09)mm
